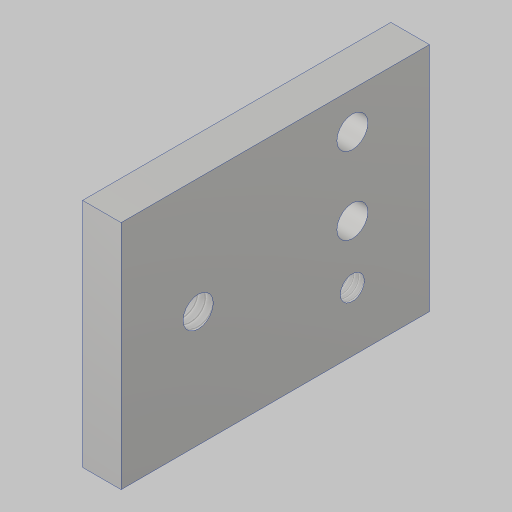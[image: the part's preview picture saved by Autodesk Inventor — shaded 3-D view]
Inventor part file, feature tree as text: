
AUTODESK INVENTOR PART (.ipt)
format: ipt  version: 2023.5 (Build 275446000, 446)  size: 113,664 bytes
history: native  units: in
note: dims shown in document units (in); Inventor stores cm internally (conversion verified against a paired STEP export)
features: sketch x3, hole x3, extrude x1
ambient origin geometry x8: Origin, YZ Plane, XZ Plane, XY Plane, X Axis, Y Axis, Z Axis, Center Point
bodies: Solid1 (feature_tree)
feature tree (7):
  extrude  "Extrusion1"  Depth=2.0in
  sketch  "Sketch2"  dims[d2=0.25in d3=0.0in d4=0.5in]
  hole  "Hole1"  [1 undecoded]
  hole  "Hole2"  [1 undecoded]
  hole  "Hole3"  [1 undecoded]
  sketch  "Sketch1"  dims[d0=1.5in d1=2.0in]
  sketch  "Sketch3"  dims[d5=0.375in d6=0.24in d7=0.5in d8=0.201in d9=0.75in d10=0.385in d11=0.25in d12=0.5635in d13=1.0in d14=0.8108in d15=0.156in d16=0.38in d17=0.375in d18=0.25in d19=0.5635in d20=1.0in d21=0.8108in d22=0.5in d23=0.196in d24=0.5in d25=0.375in d26=0.25in d27=0.5635in d28=1.0in d29=0.8108in]
note: 3 required parameter values undecoded (feature->parameter linkage not recoverable at this tier; creation-order binding heuristic only, values carry confidence <= 0.55)
